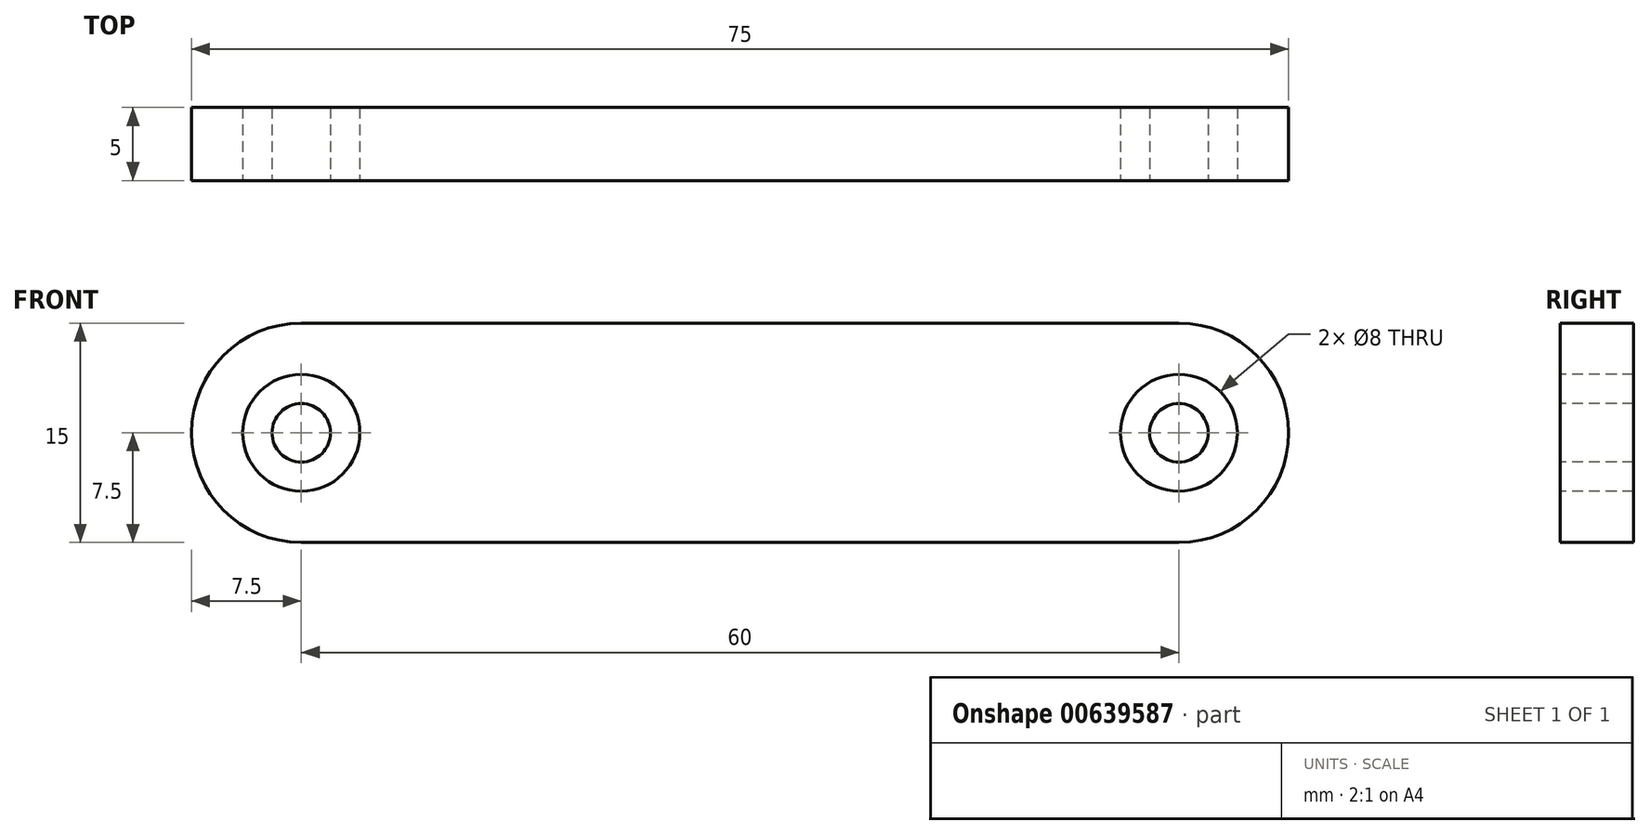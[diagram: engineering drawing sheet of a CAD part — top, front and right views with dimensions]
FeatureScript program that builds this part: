
annotation { "Feature Type Name" : "Feature", "Feature Type Description" : "" }
export const myFeature = defineFeature(function(context is Context, id is Id, definition is map)
    precondition{}
    {
        {
            var Q0;
            Q0=qCreatedBy(makeId("Front.planeOp"),FACE);
            var sketch = newSketch(context, id + "F0", { "sketchPlane" : qUnion([Q0])});
            skArc(sketch, "E0", {"start": v(0, 7.5) * mm, "mid": v(-7.5, 0) * mm, "end": v(0, -7.5) * mm});
            skArc(sketch, "E1", {"start": v(60, -7.5) * mm, "mid": v(67.5, 0) * mm, "end": v(60, 7.5) * mm});
            skLineSegment(sketch, "E2", {"start": v(0, 0) * mm, "end": v(60, 0) * mm});
            skLineSegment(sketch, "E3", {"start": v(0, 7.5) * mm, "end": v(60, 7.5) * mm});
            skLineSegment(sketch, "E4", {"start": v(0, -7.5) * mm, "end": v(60, -7.5) * mm});
            skCircle(sketch, "E5", {"center": v(0, 0) * mm, "radius": 4 * mm});
            skCircle(sketch, "E6", {"center": v(60, 0) * mm, "radius": 4 * mm});
            skSolve(sketch);
        }
        {
            var Q0;
            Q0=makeQuery(id+"F0.imprint","IMPRINT",FACE,{"disambiguationData":[TD([[makeQuery(id+"F0.imprint","IMPRINT",EDGE,{"derivedFrom":sQuery(id+"F0.wireOp",EDGE,"E0")}),1.0]])]});
            extrude(context, id + "F1", {"entities" : qUnion([Q0]), "oppositeDirection" : true, "depth" : 5 * mm, "offsetDistance" : 25.4 * mm});
        }
        {
            var Q0;
            Q0=makeQuery(id+"F1.opExtrude","CAP_FACE",FACE,{"disambiguationData":[OSD([sQuery(id+"F0.wireOp",EDGE,"E0"),sQuery(id+"F0.wireOp",EDGE,"E1"),sQuery(id+"F0.wireOp",EDGE,"E3"),sQuery(id+"F0.wireOp",EDGE,"E4"),sQuery(id+"F0.wireOp",EDGE,"E5"),sQuery(id+"F0.wireOp",EDGE,"E6")])],"isStart":true});
            var sketch = newSketch(context, id + "F2", { "sketchPlane" : qUnion([Q0])});
            skCircle(sketch, "E7", {"center": v(0, 0) * mm, "radius": 2 * mm});
            skCircle(sketch, "E8", {"center": v(60, 0) * mm, "radius": 2 * mm});
            skSolve(sketch);
        }
        {
            var Q0;
            Q0=makeQuery(id+"F2.imprint","IMPRINT",FACE,{"disambiguationData":[TD([[makeQuery(id+"F2.imprint","IMPRINT",EDGE,{"derivedFrom":sQuery(id+"F2.wireOp",EDGE,"E7")}),1.0]])]});
            var Q1;
            Q1=makeQuery(id+"F2.imprint","IMPRINT",FACE,{"disambiguationData":[TD([[makeQuery(id+"F2.imprint","IMPRINT",EDGE,{"derivedFrom":sQuery(id+"F2.wireOp",EDGE,"E8")}),1.0]])]});
            extrude(context, id + "F3", {"entities" : qUnion([Q0, Q1]), "oppositeDirection" : true, "depth" : 5 * mm, "offsetDistance" : 25.4 * mm});
        }
    });
